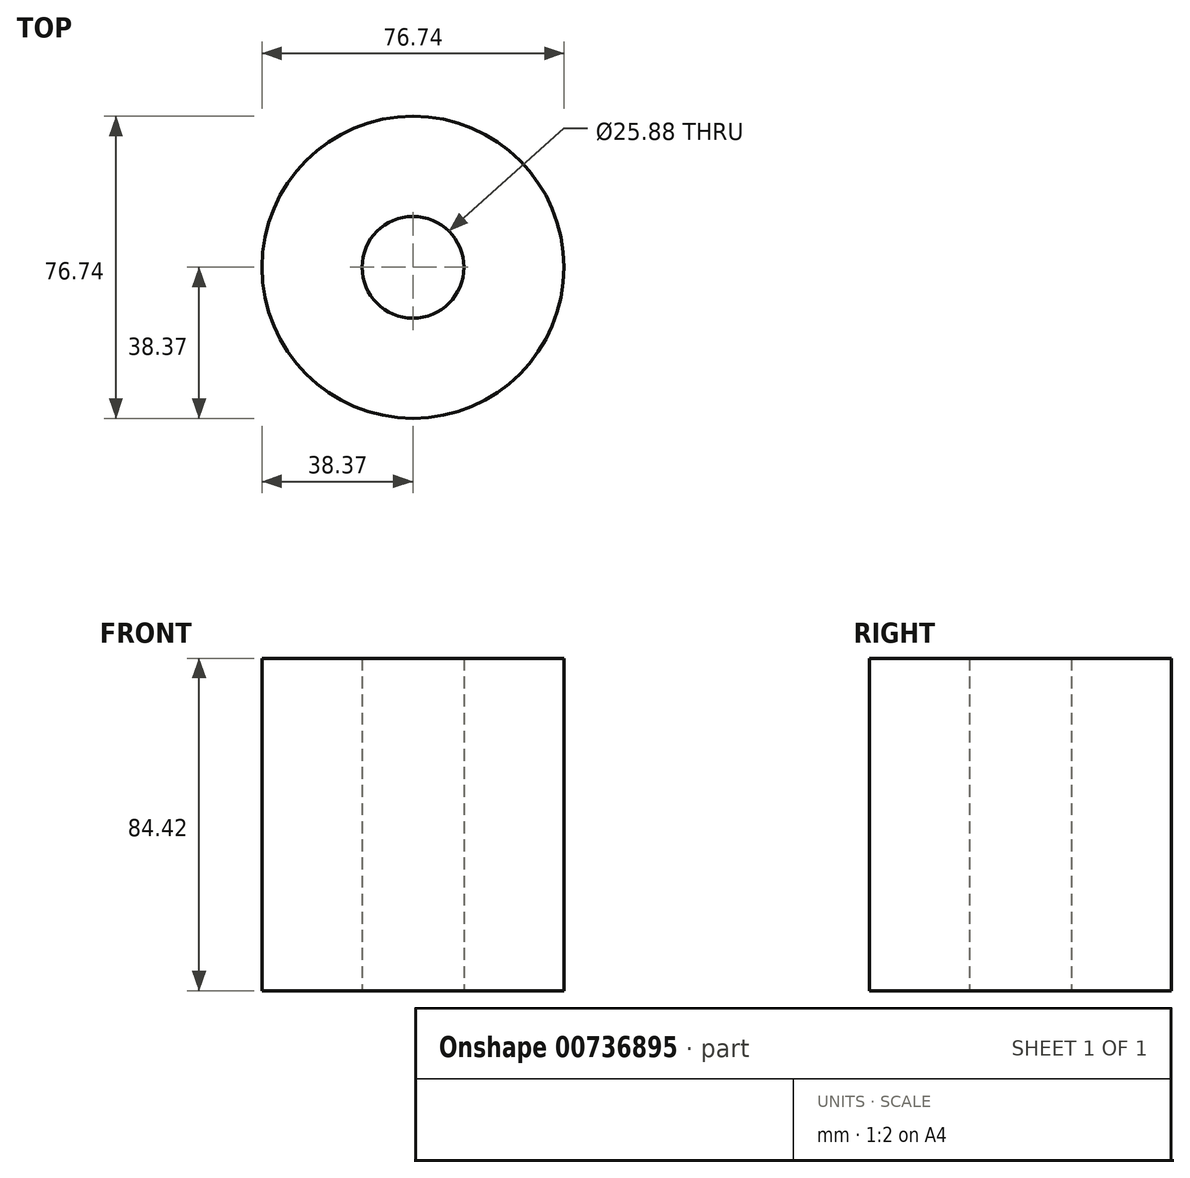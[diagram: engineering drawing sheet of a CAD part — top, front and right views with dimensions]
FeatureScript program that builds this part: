
annotation { "Feature Type Name" : "Feature", "Feature Type Description" : "" }
export const myFeature = defineFeature(function(context is Context, id is Id, definition is map)
    precondition{}
    {
        {
            var Q0;
            Q0=qCreatedBy(makeId("Top.planeOp"),FACE);
            var sketch = newSketch(context, id + "F0", { "sketchPlane" : qUnion([Q0])});
            skCircle(sketch, "E0", {"center": v(0, 0) * mm, "radius": 38.37 * mm});
            skSolve(sketch);
        }
        {
            var Q0;
            Q0=makeQuery(id+"F0.imprint","IMPRINT",FACE,{"disambiguationData":[TD([[makeQuery(id+"F0.imprint","IMPRINT",EDGE,{"derivedFrom":sQuery(id+"F0.wireOp",EDGE,"E0")}),1.0]])]});
            var sketch = newSketch(context, id + "F1", { "sketchPlane" : qUnion([Q0])});
            skCircle(sketch, "E1", {"center": v(0, 0) * mm, "radius": 12.94 * mm});
            skSolve(sketch);
        }
        {
            var Q0;
            Q0=makeQuery(id+"F1.imprint","IMPRINT",FACE,{"disambiguationData":[TD([[makeQuery(id+"F1.imprint","IMPRINT",EDGE,{"derivedFrom":sQuery(id+"F1.wireOp",EDGE,"E1")}),-1.0]])]});
            extrude(context, id + "F2", {"entities" : qUnion([Q0]), "depth" : 84.42 * mm, "offsetDistance" : 25.4 * mm});
        }
    });
